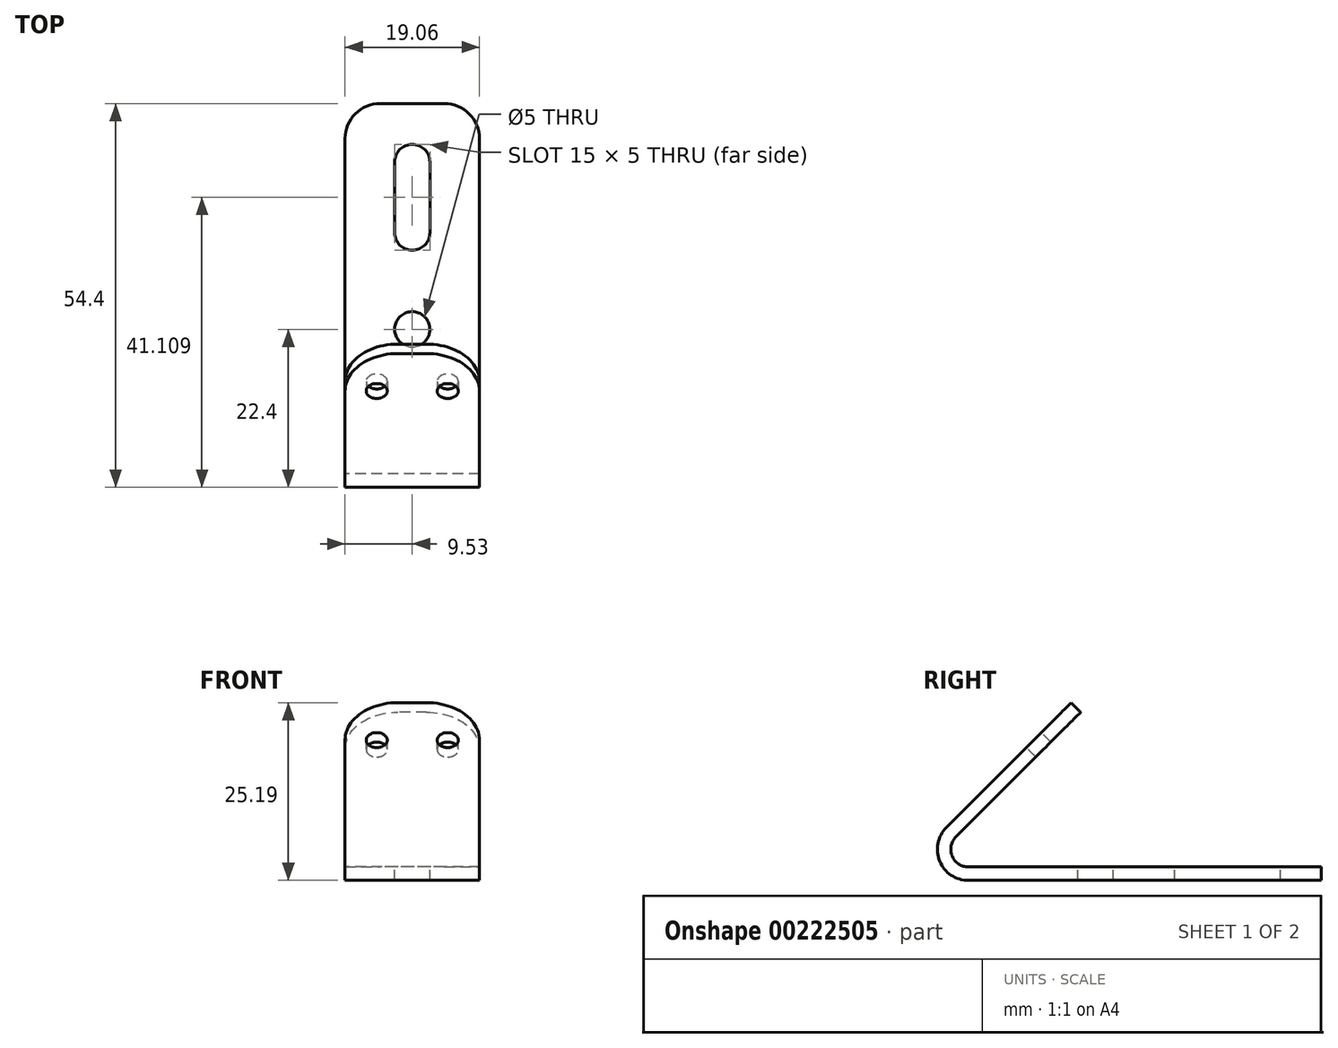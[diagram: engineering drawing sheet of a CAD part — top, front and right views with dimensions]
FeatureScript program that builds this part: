
annotation { "Feature Type Name" : "Feature", "Feature Type Description" : "" }
export const myFeature = defineFeature(function(context is Context, id is Id, definition is map)
    precondition{}
    {
        {
            var Q0;
            Q0=qCreatedBy(makeId("Right.planeOp"),FACE);
            var sketch = newSketch(context, id + "F0", { "sketchPlane" : qUnion([Q0])});
            skLineSegment(sketch, "E0", {"start": v(0, 0) * mm, "end": v(50, 0) * mm});
            skLineSegment(sketch, "E1", {"start": v(50, 0) * mm, "end": v(50, 1.9) * mm});
            skLineSegment(sketch, "E2", {"start": v(50, 1.9) * mm, "end": v(0, 1.9) * mm});
            skLineSegment(sketch, "E3", {"start": v(0, 0) * mm, "end": v(0, 4.4) * mm, "construction": true});
            skArc(sketch, "E4", {"start": v(-3.11, 7.51) * mm, "mid": v(-4.07, 2.72) * mm, "end": v(0, 0) * mm});
            skLineSegment(sketch, "E5", {"start": v(-3.11, 7.51) * mm, "end": v(1.25, 3.15) * mm, "construction": true});
            skLineSegment(sketch, "E6", {"start": v(-3.11, 7.51) * mm, "end": v(14.57, 25.19) * mm});
            skLineSegment(sketch, "E7", {"start": v(14.57, 25.19) * mm, "end": v(15.9, 23.85) * mm});
            skLineSegment(sketch, "E8", {"start": v(15.9, 23.85) * mm, "end": v(-1.77, 6.17) * mm});
            skArc(sketch, "E9.0", {"start": v(-1.77, 6.17) * mm, "mid": v(-2.3, 3.44) * mm, "end": v(0, 1.9) * mm});
            skSolve(sketch);
        }
        {
            var Q0;
            Q0=makeQuery(id+"F0.imprint","IMPRINT",FACE,{"disambiguationData":[TD([[makeQuery(id+"F0.imprint","IMPRINT",EDGE,{"derivedFrom":sQuery(id+"F0.wireOp",EDGE,"E0")}),1.0]])]});
            extrude(context, id + "F1", {"entities" : qUnion([Q0]), "endBound" : BoundingType.SYMMETRIC, "depth" : 19.05 * mm});
        }
        {
            var Q0;
            Q0=makeQuery(id+"F1.opExtrude","SWEPT_FACE",FACE,{"disambiguationData":[OSD([sQuery(id+"F0.wireOp",EDGE,"E2")])]});
            var sketch = newSketch(context, id + "F2", { "sketchPlane" : qUnion([Q0])});
            skLineSegment(sketch, "E10", {"start": v(0, 57.17) * mm, "end": v(0, -14.1) * mm, "construction": true});
            skArc(sketch, "E11", {"start": v(2.5, 41.7) * mm, "mid": v(0, 44.2) * mm, "end": v(-2.5, 41.7) * mm});
            skArc(sketch, "E12", {"start": v(-2.5, 31.7) * mm, "mid": v(0, 29.2) * mm, "end": v(2.5, 31.7) * mm});
            skCircle(sketch, "E13", {"center": v(0, 18) * mm, "radius": 2.5 * mm});
            skLineSegment(sketch, "E14", {"start": v(-2.5, 41.7) * mm, "end": v(-2.5, 31.7) * mm});
            skLineSegment(sketch, "E15.MirrorCS", {"start": v(2.5, 41.7) * mm, "end": v(2.5, 31.7) * mm});
            skSolve(sketch);
        }
        {
            var Q0;
            Q0=makeQuery(id+"F2.imprint","IMPRINT",FACE,{"disambiguationData":[TD([[makeQuery(id+"F2.imprint","IMPRINT",EDGE,{"derivedFrom":sQuery(id+"F2.wireOp",EDGE,"E13")}),1.0]])]});
            var Q1;
            Q1=makeQuery(id+"F2.imprint","IMPRINT",FACE,{"disambiguationData":[TD([[makeQuery(id+"F2.imprint","IMPRINT",EDGE,{"derivedFrom":sQuery(id+"F2.wireOp",EDGE,"E11")}),1.0]])]});
            extrude(context, id + "F3", {"entities" : qUnion([Q0, Q1]), "operationType" : NewBodyOperationType.REMOVE, "endBound" : BoundingType.THROUGH_ALL, "oppositeDirection" : true, "depth" : 25 * mm});
        }
        {
            var Q0;
            Q0=makeQuery(id+"F1.opExtrude","SWEPT_FACE",FACE,{"disambiguationData":[OSD([sQuery(id+"F0.wireOp",EDGE,"E6")])]});
            var sketch = newSketch(context, id + "F4", { "sketchPlane" : qUnion([Q0])});
            skCircle(sketch, "E16", {"center": v(-5.03, 20.61) * mm, "radius": 1.5 * mm});
            skCircle(sketch, "E17", {"center": v(5.03, 20.61) * mm, "radius": 1.5 * mm});
            skSolve(sketch);
        }
        {
            var Q0;
            Q0=makeQuery(id+"F4.imprint","IMPRINT",FACE,{"disambiguationData":[TD([[makeQuery(id+"F4.imprint","IMPRINT",EDGE,{"derivedFrom":sQuery(id+"F4.wireOp",EDGE,"E16")}),1.0]])]});
            var Q1;
            Q1=makeQuery(id+"F4.imprint","IMPRINT",FACE,{"disambiguationData":[TD([[makeQuery(id+"F4.imprint","IMPRINT",EDGE,{"derivedFrom":sQuery(id+"F4.wireOp",EDGE,"E17")}),1.0]])]});
            extrude(context, id + "F5", {"entities" : qUnion([Q0, Q1]), "operationType" : NewBodyOperationType.REMOVE, "oppositeDirection" : true, "depth" : 1.9 * mm});
        }
        {
            var Q0;
            Q0=makeQuery(id+"F1.opExtrude","CAP_EDGE",EDGE,{"disambiguationData":[OSD([sQuery(id+"F0.wireOp",EDGE,"E7")])],"isStart":false});
            var Q1;
            Q1=makeQuery(id+"F1.opExtrude","CAP_EDGE",EDGE,{"disambiguationData":[OSD([sQuery(id+"F0.wireOp",EDGE,"E7")])],"isStart":true});
            fillet(context, id + "F6", {"entities" : qUnion([Q0, Q1]), "radius" : 7.5 * mm, "tangentPropagation" : true, "allowEdgeOverflow" : false});
        }
        {
            var Q0;
            Q0=makeQuery(id+"F1.opExtrude","CAP_EDGE",EDGE,{"disambiguationData":[OSD([sQuery(id+"F0.wireOp",EDGE,"E1")])],"isStart":true});
            var Q1;
            Q1=makeQuery(id+"F1.opExtrude","CAP_EDGE",EDGE,{"disambiguationData":[OSD([sQuery(id+"F0.wireOp",EDGE,"E1")])],"isStart":false});
            fillet(context, id + "F7", {"entities" : qUnion([Q0, Q1]), "radius" : 5 * mm, "tangentPropagation" : true, "allowEdgeOverflow" : false});
        }
    });
